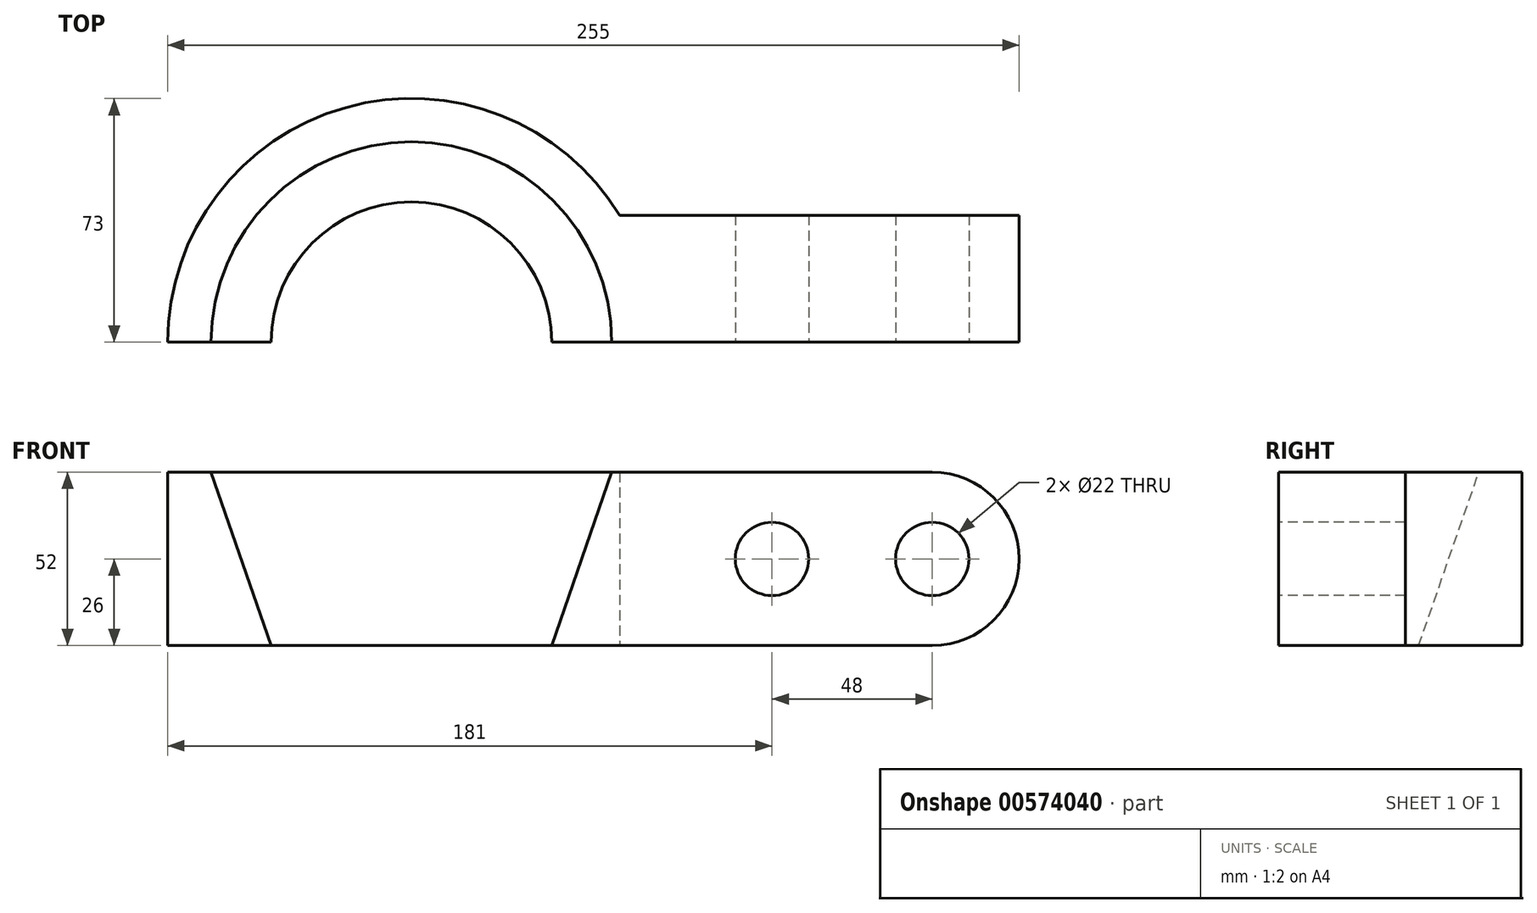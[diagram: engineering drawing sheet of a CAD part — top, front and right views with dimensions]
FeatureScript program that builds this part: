
annotation { "Feature Type Name" : "Feature", "Feature Type Description" : "" }
export const myFeature = defineFeature(function(context is Context, id is Id, definition is map)
    precondition{}
    {
        {
            var Q0;
            Q0=qCreatedBy(makeId("Top.planeOp"),FACE);
            var sketch = newSketch(context, id + "F0", { "sketchPlane" : qUnion([Q0])});
            skArc(sketch, "E0", {"start": v(42, 0) * mm, "mid": v(0, 42) * mm, "end": v(-42, 0) * mm});
            skArc(sketch, "E1", {"start": v(62.33, 38) * mm, "mid": v(-19.73, 70.28) * mm, "end": v(-73, 0) * mm});
            skLineSegment(sketch, "E2.bottom", {"start": v(62.33, 38) * mm, "end": v(182, 38) * mm});
            skLineSegment(sketch, "E2.top", {"start": v(42, 0) * mm, "end": v(182, 0) * mm});
            skLineSegment(sketch, "E2.right", {"start": v(182, 38) * mm, "end": v(182, 0) * mm});
            skLineSegment(sketch, "E3", {"start": v(-73, 0) * mm, "end": v(-42, 0) * mm});
            skSolve(sketch);
        }
        {
            var Q0;
            Q0=makeQuery(id+"F0.imprint","IMPRINT",FACE,{"disambiguationData":[TD([[makeQuery(id+"F0.imprint","IMPRINT",EDGE,{"derivedFrom":sQuery(id+"F0.wireOp",EDGE,"E0")}),-1.0]])]});
            extrude(context, id + "F1", {"entities" : qUnion([Q0]), "depth" : 52 * mm, "offsetDistance" : 25 * mm});
        }
        {
            var Q0;
            Q0=makeQuery(id+"F1.opExtrude","SWEPT_FACE",FACE,{"disambiguationData":[OSD([sQuery(id+"F0.wireOp",EDGE,"E3")])]});
            var sketch = newSketch(context, id + "F2", { "sketchPlane" : qUnion([Q0])});
            skLineSegment(sketch, "E4", {"start": v(0, 52) * mm, "end": v(-60, 52) * mm});
            skLineSegment(sketch, "E5", {"start": v(-60, 52) * mm, "end": v(-42, 0) * mm});
            skLineSegment(sketch, "E6", {"start": v(0, 52) * mm, "end": v(0, 0) * mm});
            skLineSegment(sketch, "E7", {"start": v(0, 0) * mm, "end": v(-42, 0) * mm});
            skSolve(sketch);
        }
        {
            var Q0;
            Q0 = qSketchRegion(id + "F2", true);
            var Q1;
            Q1=sQuery(id+"F2.wireOp",EDGE,"E6");
            revolve(context, id + "F3", {"operationType" : NewBodyOperationType.REMOVE, "entities" : qUnion([Q0]), "axis" : qUnion([Q1]), "revolveType" : RevolveType.FULL, "oppositeDirection" : true});
        }
        {
            var Q0;
            Q0=makeQuery(id+"F1.opExtrude","SWEPT_FACE",FACE,{"disambiguationData":[OSD([sQuery(id+"F0.wireOp",EDGE,"E2.top")])]});
            var sketch = newSketch(context, id + "F4", { "sketchPlane" : qUnion([Q0])});
            skCircle(sketch, "E8", {"center": v(108, 26) * mm, "radius": 11 * mm});
            skCircle(sketch, "E9", {"center": v(156, 26) * mm, "radius": 11 * mm});
            skSolve(sketch);
        }
        {
            var Q0;
            Q0=makeQuery(id+"F4.imprint","IMPRINT",FACE,{"disambiguationData":[TD([[makeQuery(id+"F4.imprint","IMPRINT",EDGE,{"derivedFrom":sQuery(id+"F4.wireOp",EDGE,"E8")}),1.0]])]});
            var Q1;
            Q1=makeQuery(id+"F4.imprint","IMPRINT",FACE,{"disambiguationData":[TD([[makeQuery(id+"F4.imprint","IMPRINT",EDGE,{"derivedFrom":sQuery(id+"F4.wireOp",EDGE,"E9")}),1.0]])]});
            extrude(context, id + "F5", {"entities" : qUnion([Q0, Q1]), "operationType" : NewBodyOperationType.REMOVE, "oppositeDirection" : true, "depth" : 44.7 * mm, "offsetDistance" : 25 * mm});
        }
        {
            var Q0;
            Q0=makeQuery(id+"F1.opExtrude","CAP_EDGE",EDGE,{"disambiguationData":[OSD([sQuery(id+"F0.wireOp",EDGE,"E2.right")])],"isStart":false});
            var Q1;
            Q1=makeQuery(id+"F1.opExtrude","CAP_EDGE",EDGE,{"disambiguationData":[OSD([sQuery(id+"F0.wireOp",EDGE,"E2.right")])],"isStart":true});
            fillet(context, id + "F6", {"entities" : qUnion([Q0, Q1]), "radius" : 26 * mm, "tangentPropagation" : true, "allowEdgeOverflow" : false});
        }
    });
